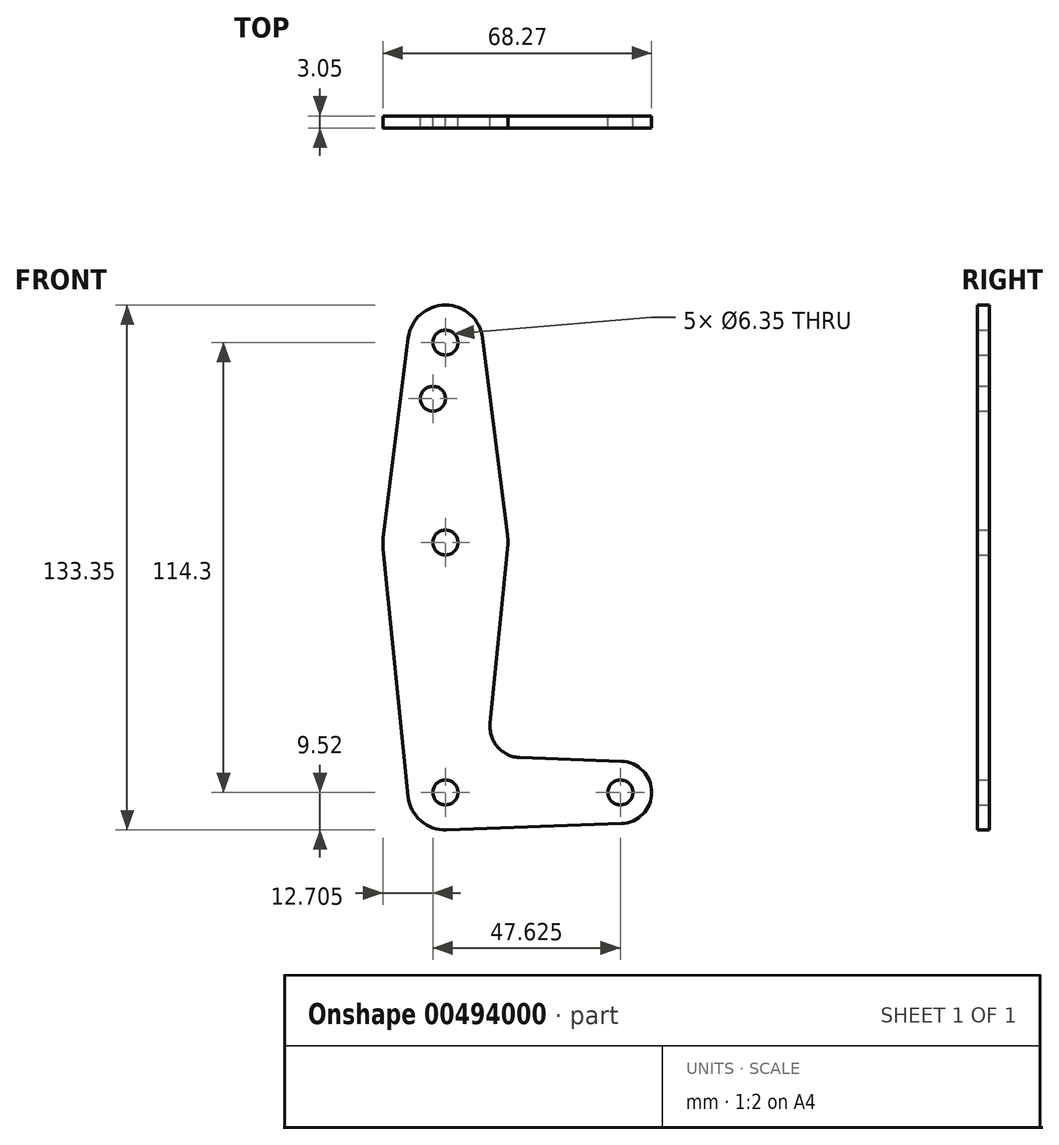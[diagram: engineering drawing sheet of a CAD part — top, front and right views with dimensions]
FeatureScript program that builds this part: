
annotation { "Feature Type Name" : "Feature", "Feature Type Description" : "" }
export const myFeature = defineFeature(function(context is Context, id is Id, definition is map)
    precondition{}
    {
        {
            var Q0;
            Q0=qCreatedBy(makeId("Front.planeOp"),FACE);
            var sketch = newSketch(context, id + "F0", { "sketchPlane" : qUnion([Q0])});
            skLineSegment(sketch, "E0", {"start": v(0, 114.3) * mm, "end": v(0, 0) * mm, "construction": true});
            skLineSegment(sketch, "E1", {"start": v(0, 0) * mm, "end": v(44.45, 0) * mm, "construction": true});
            skCircle(sketch, "E2", {"center": v(0, 114.3) * mm, "radius": 9.53 * mm});
            skCircle(sketch, "E3", {"center": v(0, 63.5) * mm, "radius": 15.88 * mm});
            skCircle(sketch, "E4", {"center": v(0, 0) * mm, "radius": 9.53 * mm});
            skCircle(sketch, "E5", {"center": v(44.45, 0) * mm, "radius": 7.94 * mm});
            skLineSegment(sketch, "E6", {"start": v(9.45, 115.5) * mm, "end": v(15.75, 65.48) * mm});
            skLineSegment(sketch, "E7", {"start": v(-9.45, 115.5) * mm, "end": v(-15.75, 65.48) * mm});
            skLineSegment(sketch, "E8", {"start": v(-15.8, 61.91) * mm, "end": v(-9.48, -0.95) * mm});
            skLineSegment(sketch, "E9", {"start": v(11.34, 17.6) * mm, "end": v(15.8, 61.91) * mm});
            skLineSegment(sketch, "E10", {"start": v(18.97, 8.85) * mm, "end": v(44.73, 7.93) * mm});
            skLineSegment(sketch, "E11", {"start": v(0.34, -9.52) * mm, "end": v(44.73, -7.93) * mm});
            skCircle(sketch, "E12", {"center": v(-3.17, 100.03) * mm, "radius": 3.18 * mm});
            skCircle(sketch, "E13", {"center": v(0, 63.5) * mm, "radius": 3.18 * mm});
            skCircle(sketch, "E14", {"center": v(0, 0) * mm, "radius": 3.18 * mm});
            skCircle(sketch, "E15", {"center": v(44.45, 0) * mm, "radius": 3.18 * mm});
            skCircle(sketch, "E16", {"center": v(0, 114.3) * mm, "radius": 3.18 * mm});
            skArc(sketch, "E17.filletArc", {"start": v(11.34, 17.6) * mm, "mid": v(13.26, 11.57) * mm, "end": v(18.97, 8.85) * mm});
            skSolve(sketch);
        }
        {
            var Q0;
            Q0 = qSketchRegion(id + "F0", true);
            extrude(context, id + "F1", {"entities" : qUnion([Q0]), "depth" : 3.05 * mm});
        }
    });
